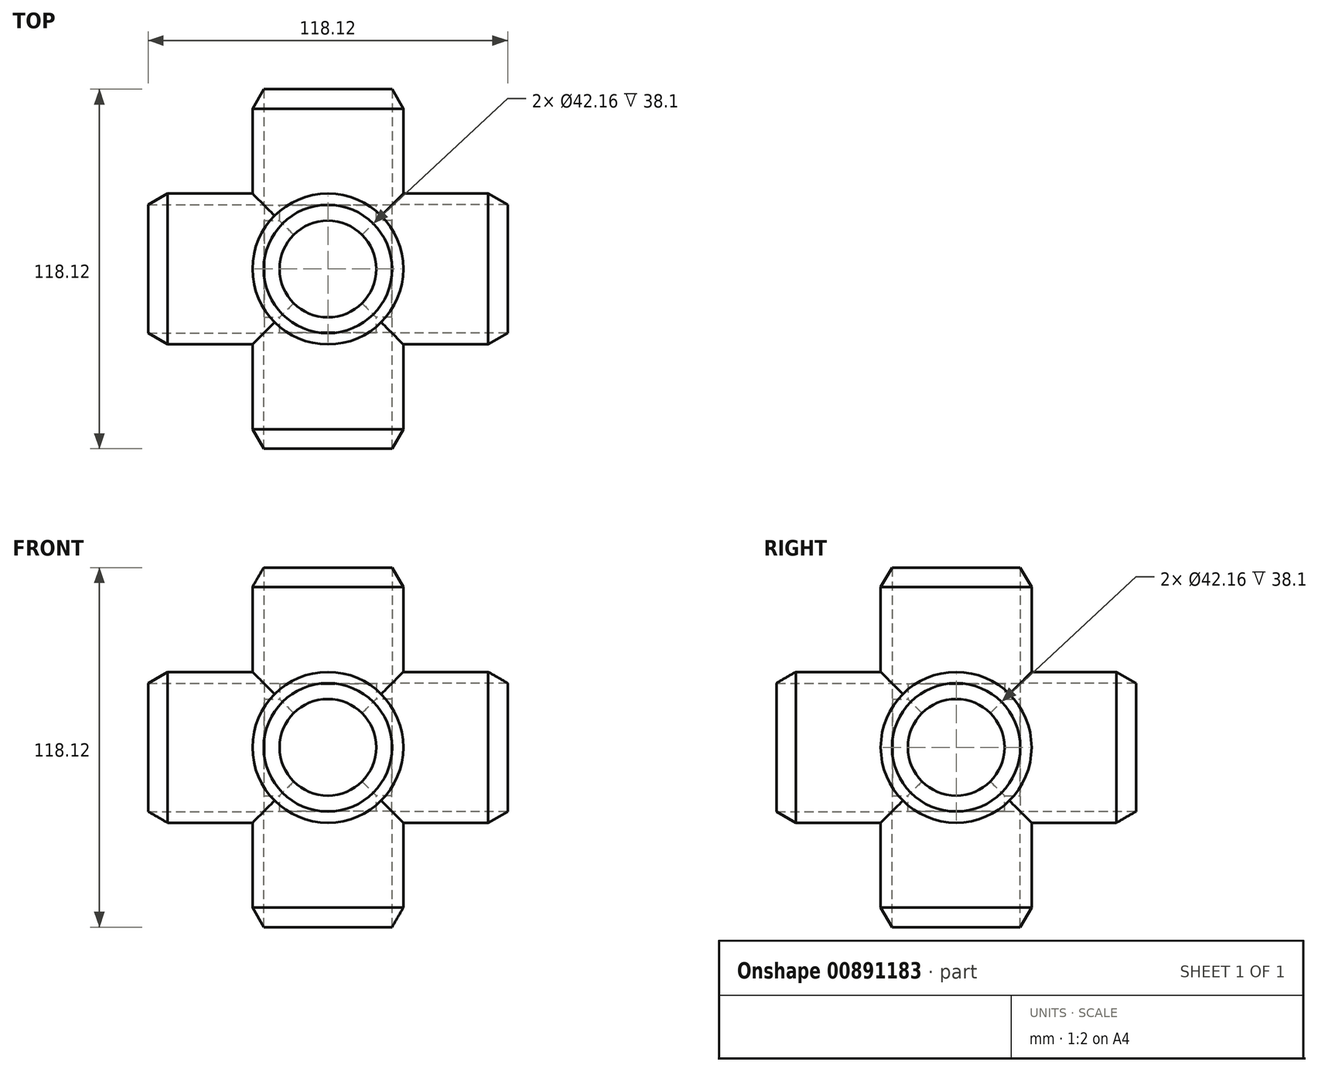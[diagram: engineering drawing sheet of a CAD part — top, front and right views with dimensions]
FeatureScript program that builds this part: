
annotation { "Feature Type Name" : "Feature", "Feature Type Description" : "" }
export const myFeature = defineFeature(function(context is Context, id is Id, definition is map)
    precondition{}
    {
        {
            var Q0;
            Q0=qCreatedBy(makeId("Right.planeOp"),FACE);
            var sketch = newSketch(context, id + "F0", { "sketchPlane" : qUnion([Q0])});
            skLineSegment(sketch, "E0", {"start": v(-59.06, 21.08) * mm, "end": v(-20.96, 21.08) * mm});
            skLineSegment(sketch, "E1", {"start": v(-20.96, 21.08) * mm, "end": v(-20.96, 15.88) * mm});
            skLineSegment(sketch, "E2", {"start": v(-20.96, 15.88) * mm, "end": v(0, 15.88) * mm});
            skLineSegment(sketch, "E3", {"start": v(15.87, 0) * mm, "end": v(15.87, 0) * mm});
            skLineSegment(sketch, "E4", {"start": v(15.87, 0) * mm, "end": v(24.77, 0) * mm});
            skLineSegment(sketch, "E5", {"start": v(24.77, 0) * mm, "end": v(24.77, 0) * mm});
            skLineSegment(sketch, "E6", {"start": v(0, 24.77) * mm, "end": v(-52.68, 24.76) * mm});
            skLineSegment(sketch, "E7", {"start": v(-52.68, 24.76) * mm, "end": v(-59.06, 21.08) * mm});
            skArc(sketch, "E8.filletArc", {"start": v(24.77, 0) * mm, "mid": v(17.51, 17.51) * mm, "end": v(0, 24.77) * mm});
            skArc(sketch, "E9.filletArc", {"start": v(15.88, 0) * mm, "mid": v(11.23, 11.23) * mm, "end": v(0, 15.88) * mm});
            skLineSegment(sketch, "E10", {"start": v(0, 0) * mm, "end": v(0, -11.7) * mm});
            skLineSegment(sketch, "E11", {"start": v(0, 0) * mm, "end": v(10.52, 0) * mm});
            skLineSegment(sketch, "E12", {"start": v(-59.06, 21.08) * mm, "end": v(-59.06, 0) * mm});
            skLineSegment(sketch, "E13", {"start": v(-59.06, 0) * mm, "end": v(15.87, 0) * mm});
            skSolve(sketch);
        }
        {
            var Q0;
            Q0=qCreatedBy(makeId("Right.planeOp"),FACE);
            var sketch = newSketch(context, id + "F1", { "sketchPlane" : qUnion([Q0])});
            skLineSegment(sketch, "E14", {"start": v(-21.08, -59.06) * mm, "end": v(-21.08, -20.96) * mm});
            skLineSegment(sketch, "E15", {"start": v(-21.08, -20.96) * mm, "end": v(-15.88, -20.96) * mm});
            skLineSegment(sketch, "E16", {"start": v(-15.88, -20.96) * mm, "end": v(-15.88, 0) * mm});
            skLineSegment(sketch, "E17", {"start": v(0, 15.88) * mm, "end": v(0, 15.88) * mm});
            skLineSegment(sketch, "E18", {"start": v(0, 15.88) * mm, "end": v(0, 24.77) * mm});
            skLineSegment(sketch, "E19", {"start": v(0, 24.77) * mm, "end": v(0, 24.77) * mm});
            skLineSegment(sketch, "E20", {"start": v(-24.77, 0) * mm, "end": v(-24.76, -52.68) * mm});
            skLineSegment(sketch, "E21", {"start": v(-24.76, -52.68) * mm, "end": v(-21.08, -59.06) * mm});
            skArc(sketch, "E22.filletArc", {"start": v(0, 24.77) * mm, "mid": v(-17.51, 17.51) * mm, "end": v(-24.77, 0) * mm});
            skArc(sketch, "E23.filletArc", {"start": v(0, 15.88) * mm, "mid": v(-11.23, 11.23) * mm, "end": v(-15.88, 0) * mm});
            skLineSegment(sketch, "E24", {"start": v(0, 36.04) * mm, "end": v(0, 0) * mm});
            skLineSegment(sketch, "E25", {"start": v(-2.18, 0) * mm, "end": v(0, 0) * mm});
            skLineSegment(sketch, "E26", {"start": v(-21.08, -59.06) * mm, "end": v(0, -59.06) * mm});
            skLineSegment(sketch, "E27", {"start": v(0, -59.06) * mm, "end": v(0, 15.88) * mm});
            skSolve(sketch);
        }
        {
            var Q0;
            Q0=qCreatedBy(makeId("Right.planeOp"),FACE);
            var sketch = newSketch(context, id + "F2", { "sketchPlane" : qUnion([Q0])});
            skLineSegment(sketch, "E28", {"start": v(59.06, -21.08) * mm, "end": v(20.96, -21.08) * mm});
            skLineSegment(sketch, "E29", {"start": v(20.96, -21.08) * mm, "end": v(20.96, -15.88) * mm});
            skLineSegment(sketch, "E30", {"start": v(20.96, -15.88) * mm, "end": v(0, -15.88) * mm});
            skLineSegment(sketch, "E31", {"start": v(-15.87, 0) * mm, "end": v(-15.87, 0) * mm});
            skLineSegment(sketch, "E32", {"start": v(-15.87, 0) * mm, "end": v(-24.77, 0) * mm});
            skLineSegment(sketch, "E33", {"start": v(-24.77, 0) * mm, "end": v(-24.77, 0) * mm});
            skLineSegment(sketch, "E34", {"start": v(0, -24.77) * mm, "end": v(52.68, -24.76) * mm});
            skLineSegment(sketch, "E35", {"start": v(52.68, -24.77) * mm, "end": v(59.06, -21.08) * mm});
            skArc(sketch, "E36.filletArc", {"start": v(-24.77, 0) * mm, "mid": v(-17.51, -17.51) * mm, "end": v(0, -24.77) * mm});
            skArc(sketch, "E37.filletArc", {"start": v(-15.88, 0) * mm, "mid": v(-11.23, -11.23) * mm, "end": v(0, -15.88) * mm});
            skLineSegment(sketch, "E38", {"start": v(0, 2.6) * mm, "end": v(0, 0) * mm});
            skLineSegment(sketch, "E39", {"start": v(0, 0) * mm, "end": v(10.52, 0) * mm});
            skLineSegment(sketch, "E40", {"start": v(59.06, -21.08) * mm, "end": v(59.06, 0) * mm});
            skLineSegment(sketch, "E41", {"start": v(59.06, 0) * mm, "end": v(-15.87, 0) * mm});
            skSolve(sketch);
        }
        {
            var Q0;
            Q0=qCreatedBy(makeId("Right.planeOp"),FACE);
            var sketch = newSketch(context, id + "F3", { "sketchPlane" : qUnion([Q0])});
            skLineSegment(sketch, "E42", {"start": v(21.08, 59.06) * mm, "end": v(21.08, 20.95) * mm});
            skLineSegment(sketch, "E43", {"start": v(21.08, 20.95) * mm, "end": v(15.88, 20.95) * mm});
            skLineSegment(sketch, "E44", {"start": v(15.88, 20.96) * mm, "end": v(15.88, 0) * mm});
            skLineSegment(sketch, "E45", {"start": v(0, -15.88) * mm, "end": v(0, -15.88) * mm});
            skLineSegment(sketch, "E46", {"start": v(0, -15.88) * mm, "end": v(0, -24.77) * mm});
            skLineSegment(sketch, "E47", {"start": v(0, -24.77) * mm, "end": v(0, -24.77) * mm});
            skLineSegment(sketch, "E48", {"start": v(24.77, 0) * mm, "end": v(24.76, 52.68) * mm});
            skLineSegment(sketch, "E49", {"start": v(24.76, 52.68) * mm, "end": v(21.08, 59.06) * mm});
            skArc(sketch, "E50.filletArc", {"start": v(0, -24.77) * mm, "mid": v(17.51, -17.51) * mm, "end": v(24.77, 0) * mm});
            skArc(sketch, "E51.filletArc", {"start": v(0, -15.88) * mm, "mid": v(11.23, -11.23) * mm, "end": v(15.88, 0) * mm});
            skLineSegment(sketch, "E52", {"start": v(0, 9.3) * mm, "end": v(0, 0) * mm});
            skLineSegment(sketch, "E53", {"start": v(-7.4, 0) * mm, "end": v(0, 0) * mm});
            skLineSegment(sketch, "E54", {"start": v(21.08, 59.05) * mm, "end": v(0, 59.05) * mm});
            skLineSegment(sketch, "E55", {"start": v(0, 59.05) * mm, "end": v(0, -15.88) * mm});
            skSolve(sketch);
        }
        {
            var Q0;
            Q0=qCreatedBy(makeId("Top.planeOp"),FACE);
            var sketch = newSketch(context, id + "F4", { "sketchPlane" : qUnion([Q0])});
            skLineSegment(sketch, "E56", {"start": v(-59.06, 21.08) * mm, "end": v(-20.96, 21.08) * mm});
            skLineSegment(sketch, "E57", {"start": v(-20.96, 21.08) * mm, "end": v(-20.96, 15.88) * mm});
            skLineSegment(sketch, "E58", {"start": v(-20.96, 15.88) * mm, "end": v(0, 15.88) * mm});
            skLineSegment(sketch, "E59", {"start": v(15.88, 0) * mm, "end": v(15.88, 0) * mm});
            skLineSegment(sketch, "E60", {"start": v(15.88, 0) * mm, "end": v(24.77, 0) * mm});
            skLineSegment(sketch, "E61", {"start": v(24.77, 0) * mm, "end": v(24.77, 0) * mm});
            skLineSegment(sketch, "E62", {"start": v(0, 24.77) * mm, "end": v(-52.68, 24.76) * mm});
            skLineSegment(sketch, "E63", {"start": v(-52.68, 24.76) * mm, "end": v(-59.06, 21.08) * mm});
            skArc(sketch, "E64.filletArc", {"start": v(24.77, 0) * mm, "mid": v(17.51, 17.51) * mm, "end": v(0, 24.77) * mm});
            skArc(sketch, "E65.filletArc", {"start": v(15.88, 0) * mm, "mid": v(11.23, 11.23) * mm, "end": v(0, 15.88) * mm});
            skLineSegment(sketch, "E66", {"start": v(0, 15.42) * mm, "end": v(0, 0) * mm});
            skLineSegment(sketch, "E67", {"start": v(-12.56, 0) * mm, "end": v(0, 0) * mm});
            skLineSegment(sketch, "E68", {"start": v(-59.06, 21.08) * mm, "end": v(-59.06, 0) * mm});
            skLineSegment(sketch, "E69", {"start": v(-59.06, 0) * mm, "end": v(15.87, 0) * mm});
            skSolve(sketch);
        }
        {
            var Q0;
            Q0=qCreatedBy(makeId("Top.planeOp"),FACE);
            var sketch = newSketch(context, id + "F5", { "sketchPlane" : qUnion([Q0])});
            skLineSegment(sketch, "E70", {"start": v(59.06, -21.08) * mm, "end": v(20.96, -21.08) * mm});
            skLineSegment(sketch, "E71", {"start": v(20.96, -21.08) * mm, "end": v(20.96, -15.88) * mm});
            skLineSegment(sketch, "E72", {"start": v(20.96, -15.88) * mm, "end": v(0, -15.88) * mm});
            skLineSegment(sketch, "E73", {"start": v(-15.87, 0) * mm, "end": v(-15.87, 0) * mm});
            skLineSegment(sketch, "E74", {"start": v(-15.87, 0) * mm, "end": v(-24.77, 0) * mm});
            skLineSegment(sketch, "E75", {"start": v(-24.77, 0) * mm, "end": v(-24.77, 0) * mm});
            skLineSegment(sketch, "E76", {"start": v(0, -24.77) * mm, "end": v(52.68, -24.76) * mm});
            skLineSegment(sketch, "E77", {"start": v(52.68, -24.76) * mm, "end": v(59.06, -21.08) * mm});
            skArc(sketch, "E78.filletArc", {"start": v(-24.77, 0) * mm, "mid": v(-17.51, -17.51) * mm, "end": v(0, -24.77) * mm});
            skArc(sketch, "E79.filletArc", {"start": v(-15.87, 0) * mm, "mid": v(-11.23, -11.23) * mm, "end": v(0, -15.88) * mm});
            skLineSegment(sketch, "E80", {"start": v(0, 0) * mm, "end": v(0, -21.33) * mm});
            skLineSegment(sketch, "E81", {"start": v(0, 0) * mm, "end": v(30.32, 0) * mm});
            skLineSegment(sketch, "E82", {"start": v(59.05, -21.08) * mm, "end": v(59.05, 0) * mm});
            skLineSegment(sketch, "E83", {"start": v(59.05, 0) * mm, "end": v(-15.87, 0) * mm});
            skSolve(sketch);
        }
        {
            var Q0;
            Q0=qSketchRegion(id+"F0",true);
            var Q1;
            Q1=sQuery(id+"F0.wireOp",EDGE,"E13");
            revolve(context, id + "F6", {"surfaceOperationType" : NewSurfaceOperationType.NEW, "entities" : qUnion([Q0]), "axis" : qUnion([Q1]), "revolveType" : RevolveType.FULL});
        }
        {
            var Q0;
            {var subQ4=makeQuery(id+"F1.imprint","IMPRINT",EDGE,{"derivedFrom":sQuery(id+"F1.wireOp",EDGE,"E14")});Q0=qUnion([makeQuery(id+"F1.imprint","IMPRINT",FACE,{"disambiguationData":[TD([[subQ4,1.0]])]}),makeQuery(id+"F1.imprint","IMPRINT",FACE,{"disambiguationData":[TD([[subQ4,-1.0]])]})]);}
            var Q1;
            Q1=sQuery(id+"F1.wireOp",EDGE,"E27");
            revolve(context, id + "F7", {"operationType" : NewBodyOperationType.ADD, "surfaceOperationType" : NewSurfaceOperationType.NEW, "entities" : qUnion([Q0]), "axis" : qUnion([Q1]), "revolveType" : RevolveType.FULL});
        }
        {
            var Q0;
            Q0=qSketchRegion(id+"F2",true);
            var Q1;
            Q1=sQuery(id+"F2.wireOp",EDGE,"E41");
            revolve(context, id + "F8", {"operationType" : NewBodyOperationType.ADD, "surfaceOperationType" : NewSurfaceOperationType.NEW, "entities" : qUnion([Q0]), "axis" : qUnion([Q1]), "revolveType" : RevolveType.FULL});
        }
        {
            var Q0;
            Q0=qSketchRegion(id+"F3",true);
            var Q1;
            Q1=sQuery(id+"F3.wireOp",EDGE,"E55");
            revolve(context, id + "F9", {"operationType" : NewBodyOperationType.ADD, "surfaceOperationType" : NewSurfaceOperationType.NEW, "entities" : qUnion([Q0]), "axis" : qUnion([Q1]), "revolveType" : RevolveType.FULL});
        }
        {
            var Q0;
            Q0=qSketchRegion(id+"F4",true);
            var Q1;
            Q1=sQuery(id+"F4.wireOp",EDGE,"E69");
            revolve(context, id + "F10", {"operationType" : NewBodyOperationType.ADD, "surfaceOperationType" : NewSurfaceOperationType.NEW, "entities" : qUnion([Q0]), "axis" : qUnion([Q1]), "revolveType" : RevolveType.FULL});
        }
        {
            var Q0;
            Q0=qSketchRegion(id+"F5",true);
            var Q1;
            Q1=sQuery(id+"F5.wireOp",EDGE,"E83");
            revolve(context, id + "F11", {"operationType" : NewBodyOperationType.ADD, "surfaceOperationType" : NewSurfaceOperationType.NEW, "entities" : qUnion([Q0]), "axis" : qUnion([Q1]), "revolveType" : RevolveType.FULL});
        }
        {
            var Q0;
            Q0=makeQuery(id+"F0.imprint","IMPRINT",FACE,{"disambiguationData":[TD([[makeQuery(id+"F0.imprint","IMPRINT",EDGE,{"derivedFrom":sQuery(id+"F0.wireOp",EDGE,"E0")}),-1.0]])]});
            var Q1;
            Q1=sQuery(id+"F0.wireOp",EDGE,"E13");
            revolve(context, id + "F12", {"operationType" : NewBodyOperationType.REMOVE, "surfaceOperationType" : NewSurfaceOperationType.NEW, "entities" : qUnion([Q0]), "axis" : qUnion([Q1]), "revolveType" : RevolveType.FULL, "oppositeDirection" : true});
        }
        {
            var Q0;
            Q0=makeQuery(id+"F1.imprint","IMPRINT",FACE,{"disambiguationData":[TD([[makeQuery(id+"F1.imprint","IMPRINT",EDGE,{"derivedFrom":sQuery(id+"F1.wireOp",EDGE,"E14")}),-1.0]])]});
            var Q1;
            Q1=sQuery(id+"F1.wireOp",EDGE,"E27");
            revolve(context, id + "F13", {"operationType" : NewBodyOperationType.REMOVE, "surfaceOperationType" : NewSurfaceOperationType.NEW, "entities" : qUnion([Q0]), "axis" : qUnion([Q1]), "revolveType" : RevolveType.FULL, "oppositeDirection" : true});
        }
        {
            var Q0;
            Q0=makeQuery(id+"F2.imprint","IMPRINT",FACE,{"disambiguationData":[TD([[makeQuery(id+"F2.imprint","IMPRINT",EDGE,{"derivedFrom":sQuery(id+"F2.wireOp",EDGE,"E28")}),-1.0]])]});
            var Q1;
            Q1=sQuery(id+"F2.wireOp",EDGE,"E41");
            revolve(context, id + "F14", {"operationType" : NewBodyOperationType.REMOVE, "surfaceOperationType" : NewSurfaceOperationType.NEW, "entities" : qUnion([Q0]), "axis" : qUnion([Q1]), "revolveType" : RevolveType.FULL, "oppositeDirection" : true});
        }
        {
            var Q0;
            Q0=makeQuery(id+"F3.imprint","IMPRINT",FACE,{"disambiguationData":[TD([[makeQuery(id+"F3.imprint","IMPRINT",EDGE,{"derivedFrom":sQuery(id+"F3.wireOp",EDGE,"E42")}),-1.0]])]});
            var Q1;
            Q1=sQuery(id+"F3.wireOp",EDGE,"E55");
            revolve(context, id + "F15", {"operationType" : NewBodyOperationType.REMOVE, "surfaceOperationType" : NewSurfaceOperationType.NEW, "entities" : qUnion([Q0]), "axis" : qUnion([Q1]), "revolveType" : RevolveType.FULL, "oppositeDirection" : true});
        }
        {
            var Q0;
            Q0=makeQuery(id+"F4.imprint","IMPRINT",FACE,{"disambiguationData":[TD([[makeQuery(id+"F4.imprint","IMPRINT",EDGE,{"derivedFrom":sQuery(id+"F4.wireOp",EDGE,"E56")}),-1.0]])]});
            var Q1;
            Q1=sQuery(id+"F4.wireOp",EDGE,"E69");
            revolve(context, id + "F16", {"operationType" : NewBodyOperationType.REMOVE, "surfaceOperationType" : NewSurfaceOperationType.NEW, "entities" : qUnion([Q0]), "axis" : qUnion([Q1]), "revolveType" : RevolveType.FULL, "oppositeDirection" : true});
        }
        {
            var Q0;
            Q0=makeQuery(id+"F5.imprint","IMPRINT",FACE,{"disambiguationData":[TD([[makeQuery(id+"F5.imprint","IMPRINT",EDGE,{"derivedFrom":sQuery(id+"F5.wireOp",EDGE,"E70")}),-1.0]])]});
            var Q1;
            Q1=sQuery(id+"F5.wireOp",EDGE,"E83");
            revolve(context, id + "F17", {"operationType" : NewBodyOperationType.REMOVE, "surfaceOperationType" : NewSurfaceOperationType.NEW, "entities" : qUnion([Q0]), "axis" : qUnion([Q1]), "revolveType" : RevolveType.FULL, "oppositeDirection" : true});
        }
    });
